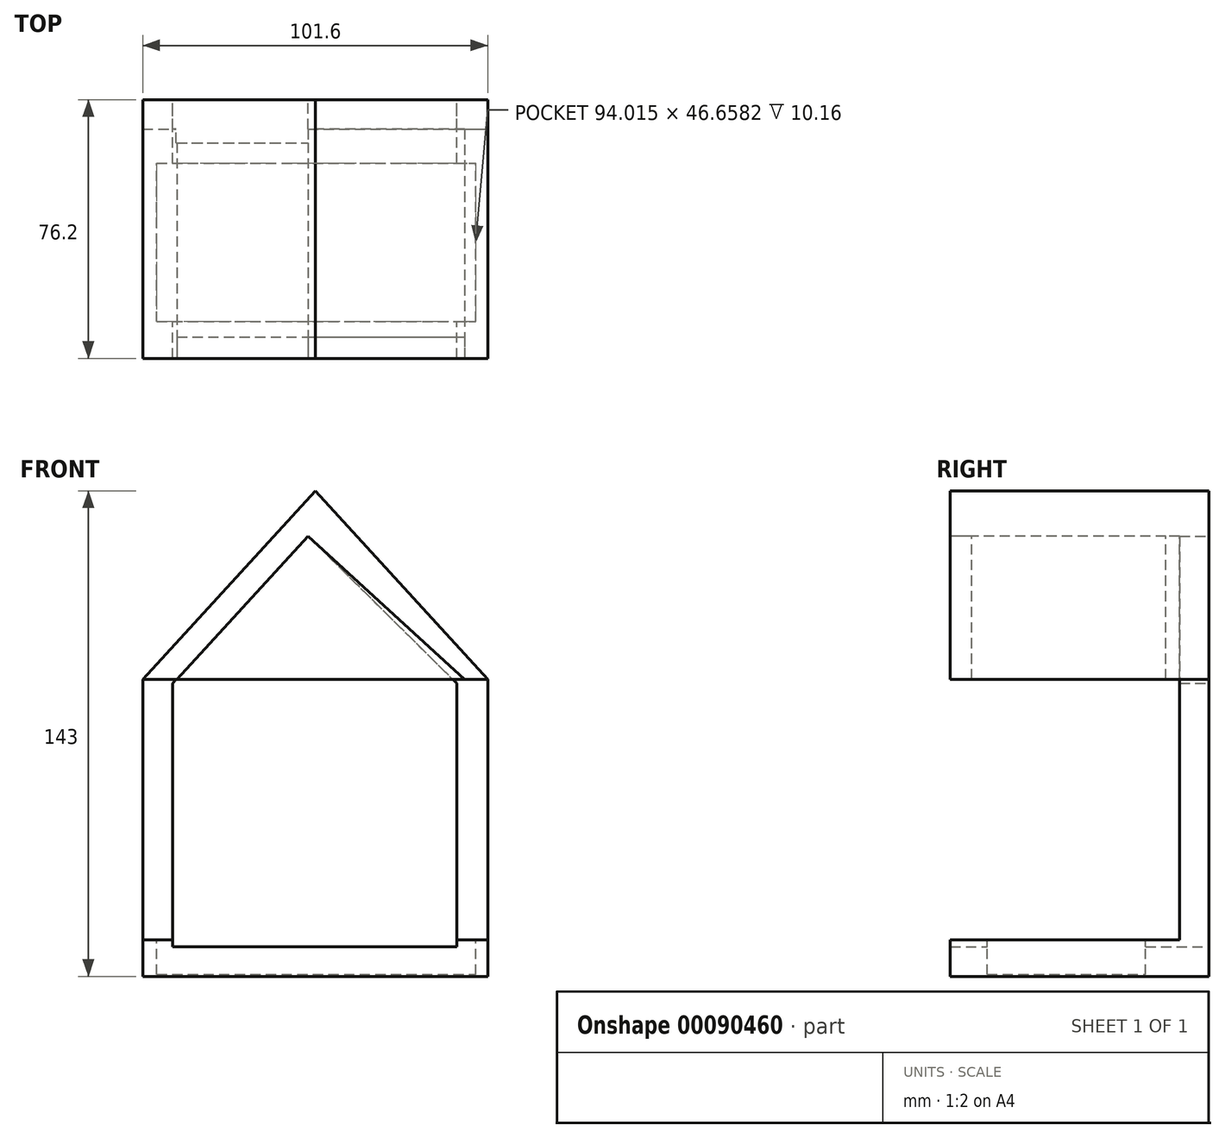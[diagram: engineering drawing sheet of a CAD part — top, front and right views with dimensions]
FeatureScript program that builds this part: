
annotation { "Feature Type Name" : "Feature", "Feature Type Description" : "" }
export const myFeature = defineFeature(function(context is Context, id is Id, definition is map)
    precondition{}
    {
        {
            var Q0;
            Q0=qCreatedBy(makeId("Front.planeOp"),FACE);
            var sketch = newSketch(context, id + "F0", { "sketchPlane" : qUnion([Q0])});
            skLineSegment(sketch, "E0.bottom", {"start": v(-48.69, -37.91) * mm, "end": v(52.91, -37.91) * mm});
            skLineSegment(sketch, "E0.top", {"start": v(-48.69, -27.23) * mm, "end": v(52.91, -27.23) * mm});
            skLineSegment(sketch, "E0.left", {"start": v(-48.69, -37.91) * mm, "end": v(-48.69, -27.23) * mm});
            skLineSegment(sketch, "E0.right", {"start": v(52.91, -37.91) * mm, "end": v(52.91, -27.23) * mm});
            skSolve(sketch);
        }
        {
            var Q0;
            Q0 = qSketchRegion(id + "F0", true);
            extrude(context, id + "F1", {"entities" : qUnion([Q0]), "depth" : 76.2 * mm});
        }
        {
            var Q0;
            Q0=qCreatedBy(makeId("Front.planeOp"),FACE);
            var sketch = newSketch(context, id + "F2", { "sketchPlane" : qUnion([Q0])});
            skLineSegment(sketch, "E1.0.0", {"start": v(-48.69, -27.23) * mm, "end": v(-48.69, -37.91) * mm});
            skLineSegment(sketch, "E1.0.1", {"start": v(-48.69, -37.91) * mm, "end": v(52.91, -37.91) * mm});
            skLineSegment(sketch, "E1.0.2", {"start": v(52.91, -37.91) * mm, "end": v(52.91, -27.23) * mm});
            skLineSegment(sketch, "E1.0.3", {"start": v(52.91, -27.23) * mm, "end": v(-48.69, -27.23) * mm});
            skLineSegment(sketch, "E2.bottom", {"start": v(-48.69, -27.23) * mm, "end": v(52.91, -27.23) * mm});
            skLineSegment(sketch, "E2.top", {"start": v(-48.69, 49.54) * mm, "end": v(52.91, 49.54) * mm});
            skLineSegment(sketch, "E2.left", {"start": v(-48.69, -27.23) * mm, "end": v(-48.69, 49.54) * mm});
            skLineSegment(sketch, "E2.right", {"start": v(52.91, -27.23) * mm, "end": v(52.91, 49.54) * mm});
            skSolve(sketch);
        }
        {
            var Q0;
            Q0 = qSketchRegion(id + "F2", true);
            extrude(context, id + "F3", {"entities" : qUnion([Q0]), "operationType" : NewBodyOperationType.ADD, "depth" : 8.7 * mm});
        }
        {
            var Q0;
            Q0=qCreatedBy(makeId("Front.planeOp"),FACE);
            var sketch = newSketch(context, id + "F4", { "sketchPlane" : qUnion([Q0])});
            skLineSegment(sketch, "E3.0.0", {"start": v(-48.69, 49.54) * mm, "end": v(-48.69, -27.23) * mm});
            skLineSegment(sketch, "E3.0.1", {"start": v(-48.69, -27.23) * mm, "end": v(52.91, -27.23) * mm});
            skLineSegment(sketch, "E3.0.2", {"start": v(52.91, -27.23) * mm, "end": v(52.91, 49.54) * mm});
            skLineSegment(sketch, "E3.0.3", {"start": v(52.91, 49.54) * mm, "end": v(-48.69, 49.54) * mm});
            skLineSegment(sketch, "E4", {"start": v(-48.69, 49.54) * mm, "end": v(2.11, 105.1) * mm});
            skLineSegment(sketch, "E5", {"start": v(2.11, 105.1) * mm, "end": v(52.91, 49.54) * mm});
            skSolve(sketch);
        }
        {
            var Q0;
            Q0=makeQuery(id+"F4.imprint","IMPRINT",FACE,{"disambiguationData":[TD([[makeQuery(id+"F4.imprint","IMPRINT",EDGE,{"derivedFrom":sQuery(id+"F4.wireOp",EDGE,"E3.0.3")}),-1.0]])]});
            extrude(context, id + "F5", {"entities" : qUnion([Q0]), "operationType" : NewBodyOperationType.ADD, "depth" : 76.2 * mm});
        }
        {
            var Q0;
            Q0=makeQuery(id+"F1.opExtrude","SWEPT_FACE",FACE,{"disambiguationData":[OSD([sQuery(id+"F0.wireOp",EDGE,"E0.top")])]});
            var sketch = newSketch(context, id + "F6", { "sketchPlane" : qUnion([Q0])});
            skLineSegment(sketch, "E6.0.0", {"start": v(58.14, 0) * mm, "end": v(58.14, -8.7) * mm});
            skLineSegment(sketch, "E6.0.1", {"start": v(58.14, -8.7) * mm, "end": v(-48.69, -8.7) * mm});
            skLineSegment(sketch, "E6.0.2", {"start": v(-48.69, -8.7) * mm, "end": v(-48.69, -76.2) * mm});
            skLineSegment(sketch, "E6.0.3", {"start": v(-48.69, -76.2) * mm, "end": v(52.91, -76.2) * mm});
            skLineSegment(sketch, "E6.0.4", {"start": v(52.91, -76.2) * mm, "end": v(52.91, 0) * mm});
            skLineSegment(sketch, "E6.0.5", {"start": v(58.14, 0) * mm, "end": v(52.91, 0) * mm});
            skLineSegment(sketch, "E7.bottom", {"start": v(-44.59, -65.38) * mm, "end": v(49.43, -65.38) * mm});
            skLineSegment(sketch, "E7.top", {"start": v(-44.59, -18.73) * mm, "end": v(49.43, -18.73) * mm});
            skLineSegment(sketch, "E7.left", {"start": v(-44.59, -65.38) * mm, "end": v(-44.59, -18.73) * mm});
            skLineSegment(sketch, "E7.right", {"start": v(49.43, -65.38) * mm, "end": v(49.43, -18.73) * mm});
            skSolve(sketch);
        }
        {
            var Q0;
            Q0=makeQuery(id+"F6.imprint","IMPRINT",FACE,{"disambiguationData":[TD([[makeQuery(id+"F6.imprint","IMPRINT",EDGE,{"derivedFrom":sQuery(id+"F6.wireOp",EDGE,"E7.bottom")}),1.0]])]});
            extrude(context, id + "F7", {"entities" : qUnion([Q0]), "operationType" : NewBodyOperationType.REMOVE, "oppositeDirection" : true, "depth" : 10.16 * mm});
        }
        {
            var Q0;
            Q0=makeQuery(id+"F5.opExtrude","CAP_FACE",FACE,{"disambiguationData":[OSD([sQuery(id+"F4.wireOp",EDGE,"E3.0.3"),sQuery(id+"F4.wireOp",EDGE,"E4"),sQuery(id+"F4.wireOp",EDGE,"E5")])],"isStart":false});
            var sketch = newSketch(context, id + "F8", { "sketchPlane" : qUnion([Q0])});
            skLineSegment(sketch, "E8.0.0", {"start": v(-48.69, 49.54) * mm, "end": v(52.91, 49.54) * mm});
            skLineSegment(sketch, "E8.0.1", {"start": v(52.91, 49.54) * mm, "end": v(2.11, 105.1) * mm});
            skLineSegment(sketch, "E8.0.2", {"start": v(2.11, 105.1) * mm, "end": v(-48.69, 49.54) * mm});
            skLineSegment(sketch, "E9", {"start": v(-38.57, 49.54) * mm, "end": v(0, 91.72) * mm});
            skLineSegment(sketch, "E10", {"start": v(0, 91.72) * mm, "end": v(46.12, 49.54) * mm});
            skLineSegment(sketch, "E11", {"start": v(46.12, 49.54) * mm, "end": v(-38.57, 49.54) * mm});
            skSolve(sketch);
        }
        {
            var Q0;
            Q0=makeQuery(id+"F8.imprint","IMPRINT",FACE,{"disambiguationData":[TD([[makeQuery(id+"F8.imprint","IMPRINT",EDGE,{"derivedFrom":sQuery(id+"F8.wireOp",EDGE,"E9")}),-1.0]])]});
            var Q1;
            Q1=makeQuery(id+"F3.opExtrude","CAP_FACE",FACE,{"disambiguationData":[OSD([sQuery(id+"F2.wireOp",EDGE,"E1.0.0"),sQuery(id+"F2.wireOp",EDGE,"E1.0.1"),sQuery(id+"F2.wireOp",EDGE,"E1.0.2"),sQuery(id+"F2.wireOp",EDGE,"E1.0.3"),sQuery(id+"F2.wireOp",EDGE,"E2.top"),sQuery(id+"F2.wireOp",EDGE,"E2.left"),sQuery(id+"F2.wireOp",EDGE,"E2.right")])],"isStart":false});
            extrude(context, id + "F9", {"entities" : qUnion([Q0]), "operationType" : NewBodyOperationType.REMOVE, "endBound" : BoundingType.UP_TO_SURFACE, "oppositeDirection" : true, "endBoundEntityFace" : qUnion([Q1]), "depth" : 25.4 * mm});
        }
        {
            var Q0;
            Q0=makeQuery(id+"F5.opExtrude","CAP_FACE",FACE,{"disambiguationData":[OSD([sQuery(id+"F4.wireOp",EDGE,"E3.0.3"),sQuery(id+"F4.wireOp",EDGE,"E4"),sQuery(id+"F4.wireOp",EDGE,"E5")])],"isStart":false});
            var sketch = newSketch(context, id + "F10", { "sketchPlane" : qUnion([Q0])});
            skLineSegment(sketch, "E12.0.0", {"start": v(-48.69, 49.54) * mm, "end": v(-38.57, 49.54) * mm});
            skLineSegment(sketch, "E12.0.1", {"start": v(-38.57, 49.54) * mm, "end": v(0, 91.72) * mm});
            skLineSegment(sketch, "E12.0.2", {"start": v(0, 91.72) * mm, "end": v(46.12, 49.54) * mm});
            skLineSegment(sketch, "E12.0.3", {"start": v(46.12, 49.54) * mm, "end": v(52.91, 49.54) * mm});
            skLineSegment(sketch, "E12.0.4", {"start": v(52.91, 49.54) * mm, "end": v(2.11, 105.1) * mm});
            skLineSegment(sketch, "E12.0.5", {"start": v(2.11, 105.1) * mm, "end": v(-48.69, 49.54) * mm});
            skLineSegment(sketch, "E13", {"start": v(-38.57, 49.54) * mm, "end": v(46.12, 49.54) * mm});
            skSolve(sketch);
        }
        {
            var Q0;
            Q0=makeQuery(id+"F10.imprint","IMPRINT",FACE,{"disambiguationData":[TD([[makeQuery(id+"F10.imprint","IMPRINT",EDGE,{"derivedFrom":sQuery(id+"F10.wireOp",EDGE,"E12.0.1")}),-1.0]])]});
            extrude(context, id + "F11", {"entities" : qUnion([Q0]), "oppositeDirection" : true, "depth" : 6.35 * mm});
        }
        {
            var Q0;
            Q0=qCreatedBy(makeId("Front.planeOp"),FACE);
            var sketch = newSketch(context, id + "F12", { "sketchPlane" : qUnion([Q0])});
            skLineSegment(sketch, "E14.bottom", {"start": v(43.8, 48.37) * mm, "end": v(-39.93, 48.37) * mm});
            skLineSegment(sketch, "E14.top", {"start": v(43.8, -29.17) * mm, "end": v(-39.93, -29.17) * mm});
            skLineSegment(sketch, "E14.left", {"start": v(43.8, 48.37) * mm, "end": v(43.8, -29.17) * mm});
            skLineSegment(sketch, "E14.right", {"start": v(-39.93, 48.37) * mm, "end": v(-39.93, -29.17) * mm});
            skSolve(sketch);
        }
        {
            var Q0;
            Q0=makeQuery(id+"F12.imprint","IMPRINT",FACE,{"disambiguationData":[TD([[makeQuery(id+"F12.imprint","IMPRINT",EDGE,{"derivedFrom":sQuery(id+"F12.wireOp",EDGE,"E14.bottom")}),1.0]])]});
            extrude(context, id + "F13", {"entities" : qUnion([Q0]), "operationType" : NewBodyOperationType.REMOVE, "endBound" : BoundingType.THROUGH_ALL, "depth" : 15.22 * mm});
        }
        {
            var Q0;
            Q0=makeQuery(id+"F5.boolean.opBoolean","MERGE",FACE,{"derivedFrom":[makeQuery(id+"F3.boolean.opBoolean","MERGE",FACE,{"derivedFrom":[makeQuery(id+"F1.opExtrude","CAP_FACE",FACE,{"disambiguationData":[OSD([sQuery(id+"F0.wireOp",EDGE,"E0.bottom"),sQuery(id+"F0.wireOp",EDGE,"E0.top"),sQuery(id+"F0.wireOp",EDGE,"E0.left"),sQuery(id+"F0.wireOp",EDGE,"E0.right")])],"isStart":true}),makeQuery(id+"F3.opExtrude","CAP_FACE",FACE,{"disambiguationData":[OSD([sQuery(id+"F2.wireOp",EDGE,"E1.0.0"),sQuery(id+"F2.wireOp",EDGE,"E1.0.1"),sQuery(id+"F2.wireOp",EDGE,"E1.0.2"),sQuery(id+"F2.wireOp",EDGE,"E2.top"),sQuery(id+"F2.wireOp",EDGE,"E2.left"),sQuery(id+"F2.wireOp",EDGE,"E2.right")])],"isStart":true})]}),makeQuery(id+"F5.opExtrude","CAP_FACE",FACE,{"disambiguationData":[OSD([sQuery(id+"F4.wireOp",EDGE,"E3.0.3"),sQuery(id+"F4.wireOp",EDGE,"E4"),sQuery(id+"F4.wireOp",EDGE,"E5")])],"isStart":true})]});
            var sketch = newSketch(context, id + "F14", { "sketchPlane" : qUnion([Q0])});
            skLineSegment(sketch, "E15", {"start": v(-43.8, 48.37) * mm, "end": v(0, 91.72) * mm});
            skLineSegment(sketch, "E16", {"start": v(39.93, 48.37) * mm, "end": v(0, 91.72) * mm});
            skLineSegment(sketch, "E17.0.0", {"start": v(0, 91.72) * mm, "end": v(38.57, 49.54) * mm});
            skLineSegment(sketch, "E17.0.2", {"start": v(38.57, 49.54) * mm, "end": v(0, 91.72) * mm});
            skSolve(sketch);
        }
        {
            var Q0;
            Q0=makeQuery(id+"F14.imprint","IMPRINT",FACE,{"disambiguationData":[TD([[makeQuery(id+"F14.imprint","IMPRINT",EDGE,{"derivedFrom":sQuery(id+"F14.wireOp",EDGE,"E15")}),-1.0]])]});
            extrude(context, id + "F15", {"entities" : qUnion([Q0]), "operationType" : NewBodyOperationType.REMOVE, "oppositeDirection" : true, "depth" : 12.7 * mm});
        }
    });
